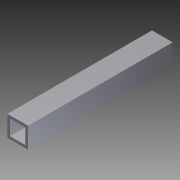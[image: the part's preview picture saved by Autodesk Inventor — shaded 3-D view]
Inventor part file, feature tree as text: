
AUTODESK INVENTOR PART (.ipt)
format: ipt  version: 2012 (Build 160160000, 160)  size: 77,824 bytes
history: native  units: in
note: dims shown in document units (in); Inventor stores cm internally (conversion verified against a paired STEP export)
features: extrude x1, sketch x1
ambient origin geometry x8: Origin, YZ Plane, XZ Plane, XY Plane, X Axis, Y Axis, Z Axis, Center Point
bodies: Solid1 (feature_tree)
feature tree (2):
  extrude  "Extrusion1"  Depth=1.0in
  sketch  "Sketch1"  dims[d0=0.5in d1=1.0in d2=1.0in d3=0.5in d4=0.125in d5=0.125in d6=0.125in d7=0.125in d8=7.0in d9=0.0in]
